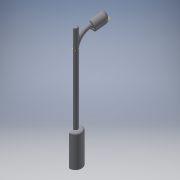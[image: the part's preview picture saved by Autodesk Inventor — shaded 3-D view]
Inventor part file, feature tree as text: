
AUTODESK INVENTOR PART (.ipt)
format: ipt  version: 2018 (Build 220112000, 112)  size: 288,768 bytes
history: native  units: in
note: dims shown in document units (in); Inventor stores cm internally (conversion verified against a paired STEP export)
features: sketch x10, other x3, plane x1
ambient origin geometry x8: Origin, YZ Plane, XZ Plane, XY Plane, X Axis, Y Axis, Z Axis, Center Point
bodies: Solid1 (feature_tree)
feature tree (14):
  other  "lampa.ipt"
  other  "Solid1::lampa.ipt"
  other  "TaggingFeature1"
  sketch  "Sketch1"  dims[d0=0.3937in]
  sketch  "Sketch6"
  sketch  "Sketch8"
  sketch  "Sketch9"
  sketch  "Sketch10"
  sketch  "Sketch11"
  sketch  "Sketch12"
  sketch  "Sketch13"
  sketch  "Sketch14"
  sketch  "Sketch15"
  plane  "Work Plane1"
